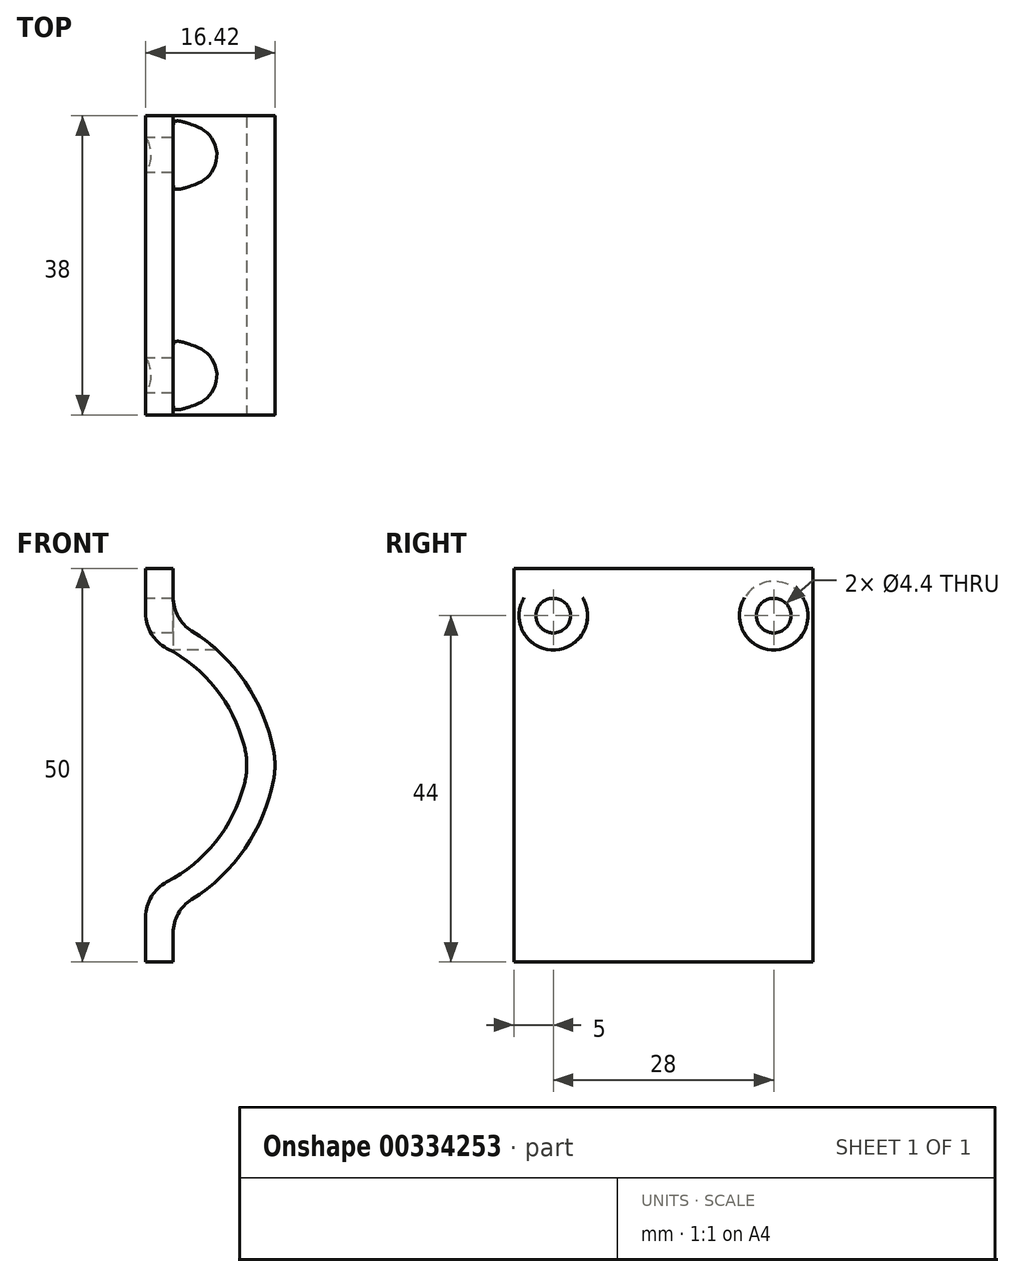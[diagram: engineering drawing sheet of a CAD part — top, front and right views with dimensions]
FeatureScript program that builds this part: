
annotation { "Feature Type Name" : "Feature", "Feature Type Description" : "" }
export const myFeature = defineFeature(function(context is Context, id is Id, definition is map)
    precondition{}
    {
        {
            var Q0;
            Q0=qCreatedBy(makeId("Front.planeOp"),FACE);
            var sketch = newSketch(context, id + "F0", { "sketchPlane" : qUnion([Q0])});
            skLineSegment(sketch, "E0", {"start": v(0, 19.28) * mm, "end": v(0, 25) * mm});
            skArc(sketch, "E1", {"start": v(13, 0) * mm, "mid": v(9.67, 8.7) * mm, "end": v(2.69, 14.84) * mm});
            skLineSegment(sketch, "E2.0", {"start": v(3.5, 21.3) * mm, "end": v(3.5, 25) * mm});
            skArc(sketch, "E2.1", {"start": v(16.52, 0) * mm, "mid": v(13.15, 9.76) * mm, "end": v(5.85, 17.06) * mm});
            skLineSegment(sketch, "E3", {"start": v(13, 0) * mm, "end": v(16.52, 0) * mm});
            skLineSegment(sketch, "E4", {"start": v(0, 25) * mm, "end": v(3.5, 25) * mm});
            skPoint(sketch, "E5", {"position": v(13, 0) * mm});
            skPoint(sketch, "E6", {"position": v(0, 20.5) * mm});
            skPoint(sketch, "E7.visualSharp", {"position": v(0, 16) * mm});
            skArc(sketch, "E7.filletArc", {"start": v(0, 19.28) * mm, "mid": v(0.72, 16.69) * mm, "end": v(2.69, 14.84) * mm});
            skPoint(sketch, "E8.visualSharp", {"position": v(3.5, 18.35) * mm});
            skArc(sketch, "E8.filletArc", {"start": v(3.5, 21.3) * mm, "mid": v(4.13, 18.88) * mm, "end": v(5.85, 17.06) * mm});
            skPoint(sketch, "E9", {"position": v(9.67, 8.7) * mm});
            skSolve(sketch);
        }
        {
            var Q0;
            Q0 = qSketchRegion(id + "F0", true);
            extrude(context, id + "F1", {"entities" : qUnion([Q0]), "endBound" : BoundingType.SYMMETRIC, "depth" : 38 * mm});
        }
        {
            var Q0;
            Q0=makeQuery(id+"F1.opExtrude","SWEPT_BODY",BODY,{"disambiguationData":[OSD([sQuery(id+"F0.wireOp",EDGE,"E0"),sQuery(id+"F0.wireOp",EDGE,"0iTDCH68-jhee-4wo7-BgfF-vNHp32cRB1C7"),sQuery(id+"F0.wireOp",EDGE,"8f49c394-f76d-41df-a19e-85d53977d136.0"),sQuery(id+"F0.wireOp",EDGE,"8f49c394-f76d-41df-a19e-85d53977d136.1"),sQuery(id+"F0.wireOp",EDGE,"wYnyYUGZ-fyma-niEf-mV2C-XKuC1QTsj6EA"),sQuery(id+"F0.wireOp",EDGE,"miDzhPnE-Xh55-hrYf-WaNm-oDuQpgmJdgPO")])]});
            var Q1;
            Q1=qCreatedBy(makeId("Top.planeOp"),FACE);
            mirror(context, id + "F2", {"operationType" : NewBodyOperationType.ADD, "entities" : qUnion([Q0]), "mirrorPlane" : qUnion([Q1])});
        }
        {
            var Q0;
            {var subQ0=makeQuery(id+"F1.opExtrude","SWEPT_EDGE",EDGE,{"disambiguationData":[OSD([sQuery(id+"F0.wireOp",EDGE,"E2.1"),sQuery(id+"F0.wireOp",EDGE,"E3")])]});Q0=makeQuery(id+"F2.boolean.opBoolean","MERGE",EDGE,{"derivedFrom":[subQ0,makeQuery(id+"F2.opPattern","COPY",EDGE,{"derivedFrom":subQ0,"instanceName":"1"})]});}
            var Q1;
            {var subQ0=makeQuery(id+"F1.opExtrude","SWEPT_EDGE",EDGE,{"disambiguationData":[OSD([sQuery(id+"F0.wireOp",EDGE,"E1"),sQuery(id+"F0.wireOp",EDGE,"E3")])]});Q1=makeQuery(id+"F2.boolean.opBoolean","MERGE",EDGE,{"derivedFrom":[subQ0,makeQuery(id+"F2.opPattern","COPY",EDGE,{"derivedFrom":subQ0,"instanceName":"1"})]});}
            fillet(context, id + "F3", {"entities" : qUnion([Q0, Q1]), "radius" : 10 * mm, "tangentPropagation" : true, "rho" : 0.5, "crossSection" : FilletCrossSection.CONIC, "allowEdgeOverflow" : false});
        }
        {
            var Q0;
            Q0=qCreatedBy(makeId("Right.planeOp"),FACE);
            var sketch = newSketch(context, id + "F4", { "sketchPlane" : qUnion([Q0])});
            skLineSegment(sketch, "E10", {"start": v(14, 19) * mm, "end": v(-14, 19) * mm});
            skPoint(sketch, "E11", {"position": v(0, 19) * mm});
            skSolve(sketch);
        }
        {
            var Q0;
            Q0=makeQuery(id+"F1.opExtrude","SWEPT_FACE",FACE,{"disambiguationData":[OSD([sQuery(id+"F0.wireOp",EDGE,"E2.0")])]});
            var sketch = newSketch(context, id + "F5", { "sketchPlane" : qUnion([Q0])});
            skPoint(sketch, "E12", {"position": v(-14, 19) * mm});
            skPoint(sketch, "E13", {"position": v(14, 19) * mm});
            skSolve(sketch);
        }
        {
            var Q0;
            Q0=sQuery(id+"F4.wireOp",VERTEX,"E10.start");
            var Q1;
            Q1=sQuery(id+"F4.wireOp",VERTEX,"E10.end");
            var Q2;
            Q2=makeQuery(id+"F1.opExtrude","SWEPT_BODY",BODY,{"disambiguationData":[OSD([sQuery(id+"F0.wireOp",EDGE,"E0"),sQuery(id+"F0.wireOp",EDGE,"E1"),sQuery(id+"F0.wireOp",EDGE,"E2.0"),sQuery(id+"F0.wireOp",EDGE,"E2.1"),sQuery(id+"F0.wireOp",EDGE,"E3"),sQuery(id+"F0.wireOp",EDGE,"E4"),sQuery(id+"F0.wireOp",EDGE,"E7.filletArc"),sQuery(id+"F0.wireOp",EDGE,"E8.filletArc")])]});
            hole(context, id + "F6", {"style" : HoleStyle.SIMPLE, "endStyle" : HoleEndStyle.THROUGH, "oppositeDirection" : true, "standardTappedOrClearance" : lookupTablePath({ "standard" : "ISO", "fit" : "Normal", "size" : "M4", "type" : "Clearance" }), "standardBlindInLast" : lookupTablePath({ "fit" : "Standard", "standard" : "ISO", "size" : "M4", "type" : "Clearance" }), "holeDiameter" : 4.4 * mm, "tappedDepth" : 3.2 * mm, "tapClearance" : 3, "locations" : qUnion([Q0, Q1]), "scope" : qUnion([Q2])});
        }
        {
            var Q0;
            Q0=sQuery(id+"F5.wireOp",VERTEX,"E12");
            var Q1;
            Q1=sQuery(id+"F5.wireOp",VERTEX,"E13");
            var Q2;
            Q2=makeQuery(id+"F1.opExtrude","SWEPT_BODY",BODY,{"disambiguationData":[OSD([sQuery(id+"F0.wireOp",EDGE,"E0"),sQuery(id+"F0.wireOp",EDGE,"E1"),sQuery(id+"F0.wireOp",EDGE,"E2.0"),sQuery(id+"F0.wireOp",EDGE,"E2.1"),sQuery(id+"F0.wireOp",EDGE,"E3"),sQuery(id+"F0.wireOp",EDGE,"E4"),sQuery(id+"F0.wireOp",EDGE,"E7.filletArc"),sQuery(id+"F0.wireOp",EDGE,"E8.filletArc")])]});
            hole(context, id + "F7", {"style" : HoleStyle.SIMPLE, "endStyle" : HoleEndStyle.THROUGH, "oppositeDirection" : true, "holeDiameter" : 8.7 * mm, "tappedDepth" : 3.75 * mm, "tapClearance" : 3, "locations" : qUnion([Q0, Q1]), "scope" : qUnion([Q2])});
        }
    });
